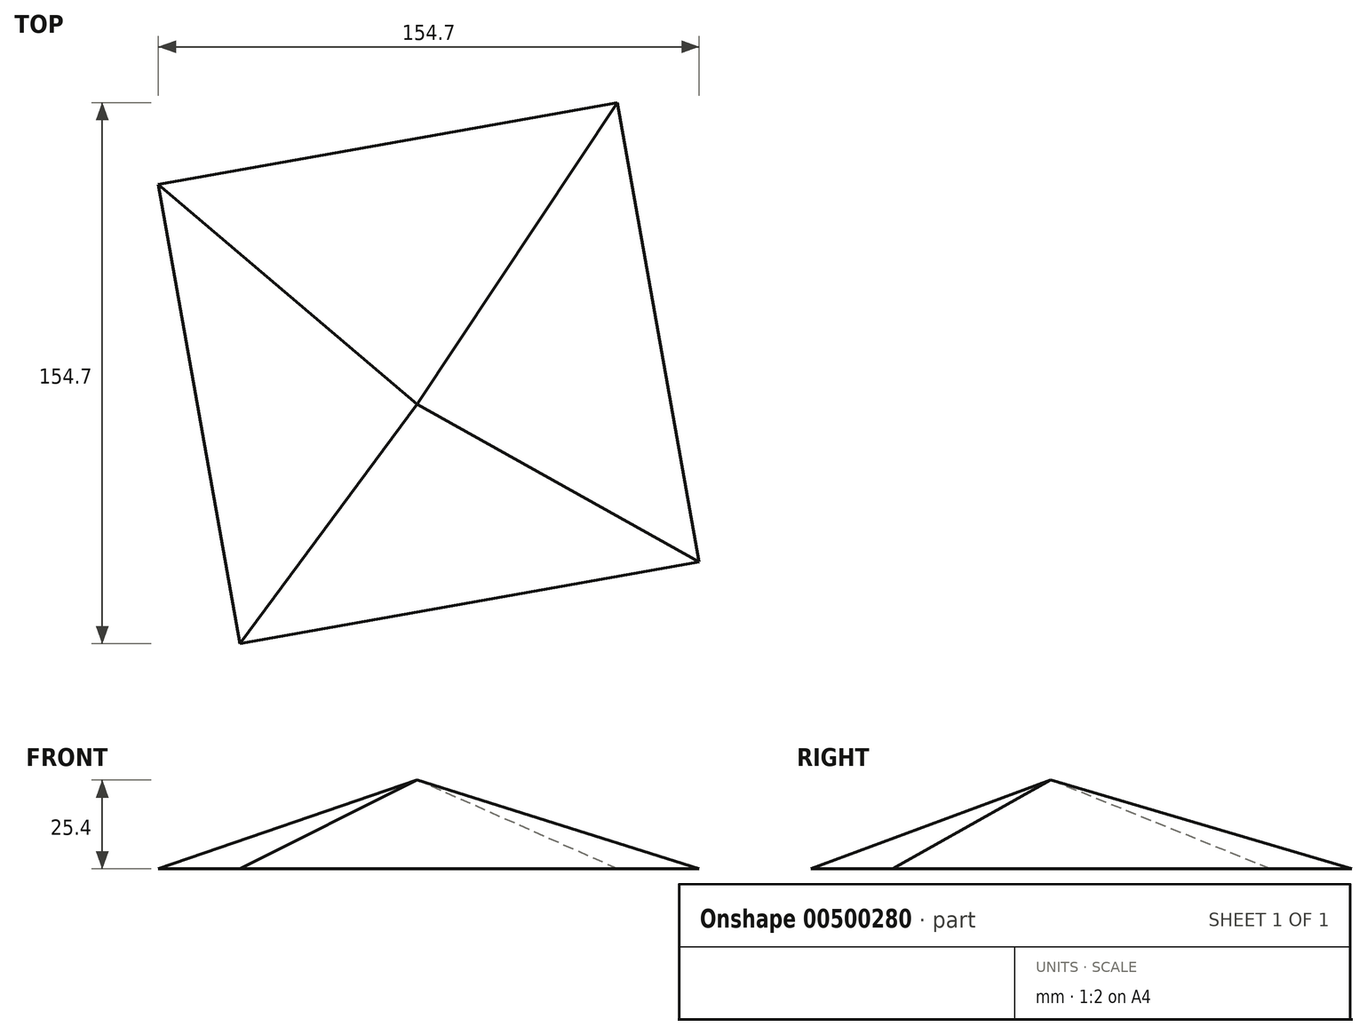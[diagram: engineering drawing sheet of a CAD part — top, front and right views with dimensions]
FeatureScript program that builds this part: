
annotation { "Feature Type Name" : "Feature", "Feature Type Description" : "" }
export const myFeature = defineFeature(function(context is Context, id is Id, definition is map)
    precondition{}
    {
        {
            var Q0;
            Q0=qCreatedBy(makeId("Top.planeOp"),FACE);
            var sketch = newSketch(context, id + "F0", { "sketchPlane" : qUnion([Q0])});
            skCircle(sketch, "E0.cCircle", {"center": v(0, 0) * mm, "radius": 94.33 * mm, "construction": true});
            skLineSegment(sketch, "E0.0", {"start": v(-77.35, 54) * mm, "end": v(54, 77.35) * mm});
            skLineSegment(sketch, "E0.1", {"start": v(54, 77.35) * mm, "end": v(77.35, -54) * mm});
            skLineSegment(sketch, "E0.2", {"start": v(77.35, -54) * mm, "end": v(-54, -77.35) * mm});
            skLineSegment(sketch, "E0.3", {"start": v(-54, -77.35) * mm, "end": v(-77.35, 54) * mm});
            skSolve(sketch);
        }
        {
            var Q0;
            Q0=makeQuery(id+"F0.imprint","IMPRINT",FACE,{"disambiguationData":[TD([[makeQuery(id+"F0.imprint","IMPRINT",EDGE,{"derivedFrom":sQuery(id+"F0.wireOp",EDGE,"E0.0")}),-1.0]])]});
            cPlane(context, id + "F1", {"entities" : qUnion([Q0]), "cplaneType" : CPlaneType.OFFSET, "offset" : 25.4 * mm, "width" : 152.4 * mm, "height" : 152.4 * mm});
        }
        {
            var Q0;
            Q0=qCreatedBy(id+"F1.planeOp",FACE);
            var sketch = newSketch(context, id + "F2", { "sketchPlane" : qUnion([Q0])});
            skLineSegment(sketch, "E1.bottom", {"start": v(-61.27, 42.12) * mm, "end": v(54.65, 42.12) * mm});
            skLineSegment(sketch, "E1.top", {"start": v(-61.27, -59.83) * mm, "end": v(54.65, -59.83) * mm});
            skLineSegment(sketch, "E1.left", {"start": v(-61.27, 42.12) * mm, "end": v(-61.27, -59.83) * mm});
            skLineSegment(sketch, "E1.right", {"start": v(54.65, 42.12) * mm, "end": v(54.65, -59.83) * mm});
            skPoint(sketch, "E1.middle", {"position": v(-3.31, -8.86) * mm});
            skSolve(sketch);
        }
        {
            var Q0;
            Q0=makeQuery(id+"F0.imprint","IMPRINT",FACE,{"disambiguationData":[TD([[makeQuery(id+"F0.imprint","IMPRINT",EDGE,{"derivedFrom":sQuery(id+"F0.wireOp",EDGE,"E0.0")}),-1.0]])]});
            var Q1;
            Q1=sQuery(id+"F2.wireOp",VERTEX,"E1.middle");
            loft(context, id + "F3", {"sheetProfilesArray" : [{ "sheetProfileEntities" : qUnion([Q0]) }, { "sheetProfileEntities" : qUnion([Q1]) }]});
        }
    });
